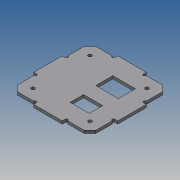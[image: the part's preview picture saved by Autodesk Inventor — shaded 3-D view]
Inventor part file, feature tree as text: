
AUTODESK INVENTOR PART (.ipt)
format: ipt  version: 2017 (Build 210142000, 142)  size: 147,456 bytes
history: native  units: mm
features: other x1, extrude x1, sketch x1
ambient origin geometry x8: Origin, YZ Plane, XZ Plane, XY Plane, X Axis, Y Axis, Z Axis, Center Point
bodies: Body1 (feature_tree)
feature tree (3):
  other  "Sólido1"
  extrude  "Extrusión1"  Depth=4.0mm
  sketch  "Boceto1"  dims[d0=40.0mm d1=4.0mm d2=2.0mm d3=110.0mm d4=118.0mm d5=4.0mm d6=8.0mm d7=5.0mm d8=80.0mm d9=80.0mm d10=24.0mm d11=32.0mm d12=31.0mm d13=71.0mm d14=3.0mm d15=20.0mm d16=19.0mm d17=27.0mm d19=24.0mm d20=4.0mm d21=0.0mm]
